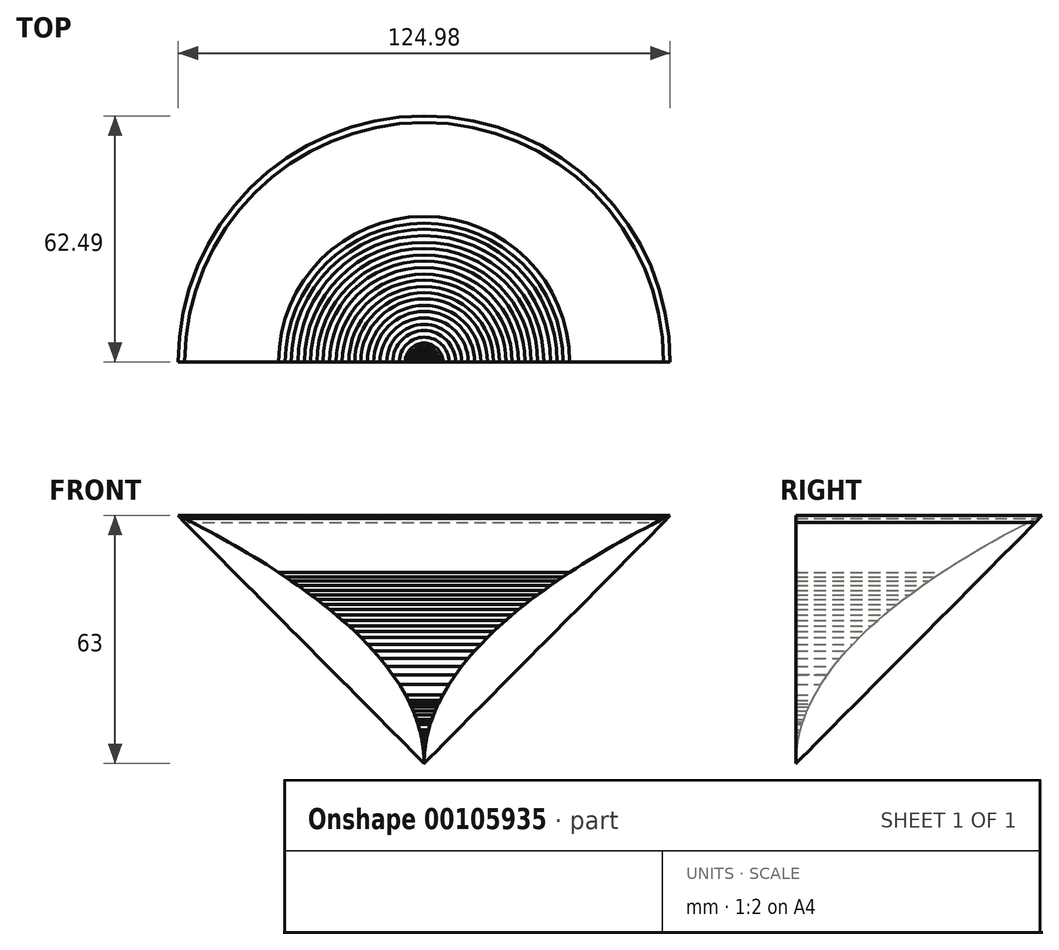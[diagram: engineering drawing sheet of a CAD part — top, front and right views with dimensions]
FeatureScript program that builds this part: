
annotation { "Feature Type Name" : "Feature", "Feature Type Description" : "" }
export const myFeature = defineFeature(function(context is Context, id is Id, definition is map)
    precondition{}
    {
        {
            var Q0;
            Q0=qCreatedBy(makeId("Front.planeOp"),FACE);
            var sketch = newSketch(context, id + "F0", { "sketchPlane" : qUnion([Q0])});
            skLineSegment(sketch, "E0", {"start": v(0, 0) * mm, "end": v(0, 71.45) * mm, "construction": true});
            skLineSegment(sketch, "E1", {"start": v(0.03, 1.24) * mm, "end": v(0.06, 1.75) * mm});
            skLineSegment(sketch, "E2", {"start": v(0.06, 1.75) * mm, "end": v(0.08, 2.15) * mm});
            skLineSegment(sketch, "E3", {"start": v(0.08, 2.15) * mm, "end": v(0.1, 2.48) * mm});
            skLineSegment(sketch, "E4", {"start": v(0.1, 2.48) * mm, "end": v(0.13, 2.77) * mm});
            skLineSegment(sketch, "E5", {"start": v(0.13, 2.77) * mm, "end": v(0.15, 3.04) * mm});
            skLineSegment(sketch, "E6", {"start": v(0.15, 3.04) * mm, "end": v(0.2, 3.5) * mm});
            skLineSegment(sketch, "E7", {"start": v(0.2, 3.5) * mm, "end": v(0.22, 3.72) * mm});
            skLineSegment(sketch, "E8", {"start": v(0.22, 3.72) * mm, "end": v(0.25, 3.92) * mm});
            skLineSegment(sketch, "E9", {"start": v(0.25, 3.92) * mm, "end": v(0.3, 4.3) * mm});
            skLineSegment(sketch, "E10", {"start": v(0.3, 4.3) * mm, "end": v(0.4, 4.96) * mm});
            skLineSegment(sketch, "E11", {"start": v(0.4, 4.96) * mm, "end": v(0.42, 5.11) * mm});
            skLineSegment(sketch, "E12", {"start": v(0.42, 5.11) * mm, "end": v(0.44, 5.26) * mm});
            skLineSegment(sketch, "E13", {"start": v(0.44, 5.26) * mm, "end": v(0.49, 5.54) * mm});
            skLineSegment(sketch, "E14", {"start": v(0.49, 5.54) * mm, "end": v(0.59, 6.07) * mm});
            skLineSegment(sketch, "E15", {"start": v(0.59, 6.07) * mm, "end": v(0.78, 7.01) * mm});
            skLineSegment(sketch, "E16", {"start": v(0.78, 7.01) * mm, "end": v(0.83, 7.23) * mm});
            skLineSegment(sketch, "E17", {"start": v(0.83, 7.23) * mm, "end": v(0.87, 7.44) * mm});
            skLineSegment(sketch, "E18", {"start": v(0.87, 7.44) * mm, "end": v(0.97, 7.84) * mm});
            skLineSegment(sketch, "E19", {"start": v(0.97, 7.84) * mm, "end": v(1.16, 8.59) * mm});
            skLineSegment(sketch, "E20", {"start": v(1.16, 8.59) * mm, "end": v(1.55, 9.92) * mm});
            skLineSegment(sketch, "E21", {"start": v(1.55, 9.92) * mm, "end": v(1.58, 10) * mm});
            skLineSegment(sketch, "E22", {"start": v(1.58, 10) * mm, "end": v(1.65, 10.25) * mm});
            skLineSegment(sketch, "E23", {"start": v(1.65, 10.25) * mm, "end": v(1.76, 10.57) * mm});
            skLineSegment(sketch, "E24", {"start": v(1.76, 10.57) * mm, "end": v(1.97, 11.18) * mm});
            skLineSegment(sketch, "E25", {"start": v(1.97, 11.18) * mm, "end": v(2.39, 12.31) * mm});
            skLineSegment(sketch, "E26", {"start": v(2.39, 12.31) * mm, "end": v(2.41, 12.38) * mm});
            skLineSegment(sketch, "E27", {"start": v(2.41, 12.38) * mm, "end": v(2.44, 12.45) * mm});
            skLineSegment(sketch, "E28", {"start": v(2.44, 12.45) * mm, "end": v(2.49, 12.58) * mm});
            skLineSegment(sketch, "E29", {"start": v(2.49, 12.58) * mm, "end": v(2.6, 12.84) * mm});
            skLineSegment(sketch, "E30", {"start": v(2.6, 12.84) * mm, "end": v(2.8, 13.35) * mm});
            skLineSegment(sketch, "E31", {"start": v(2.8, 13.35) * mm, "end": v(3.22, 14.31) * mm});
            skLineSegment(sketch, "E32", {"start": v(3.22, 14.31) * mm, "end": v(3.25, 14.37) * mm});
            skLineSegment(sketch, "E33", {"start": v(3.25, 14.37) * mm, "end": v(3.27, 14.42) * mm});
            skLineSegment(sketch, "E34", {"start": v(3.27, 14.42) * mm, "end": v(3.32, 14.53) * mm});
            skLineSegment(sketch, "E35", {"start": v(3.32, 14.53) * mm, "end": v(3.42, 14.74) * mm});
            skLineSegment(sketch, "E36", {"start": v(3.42, 14.74) * mm, "end": v(3.61, 15.16) * mm});
            skLineSegment(sketch, "E37", {"start": v(3.61, 15.16) * mm, "end": v(4, 15.96) * mm});
            skLineSegment(sketch, "E38", {"start": v(4, 15.96) * mm, "end": v(4.78, 17.45) * mm});
            skLineSegment(sketch, "E39", {"start": v(4.78, 17.45) * mm, "end": v(6.31, 20.05) * mm});
            skLineSegment(sketch, "E40", {"start": v(6.31, 20.05) * mm, "end": v(7.97, 22.53) * mm});
            skLineSegment(sketch, "E41", {"start": v(7.97, 22.53) * mm, "end": v(9.52, 24.63) * mm});
            skLineSegment(sketch, "E42", {"start": v(9.52, 24.63) * mm, "end": v(11.2, 26.71) * mm});
            skLineSegment(sketch, "E43", {"start": v(11.2, 26.71) * mm, "end": v(12.85, 28.61) * mm});
            skLineSegment(sketch, "E44", {"start": v(12.85, 28.61) * mm, "end": v(14.4, 30.28) * mm});
            skLineSegment(sketch, "E45", {"start": v(14.4, 30.28) * mm, "end": v(16.06, 31.98) * mm});
            skLineSegment(sketch, "E46", {"start": v(16.06, 31.98) * mm, "end": v(17.62, 33.5) * mm});
            skLineSegment(sketch, "E47", {"start": v(17.62, 33.5) * mm, "end": v(19.14, 34.92) * mm});
            skLineSegment(sketch, "E48", {"start": v(19.14, 34.92) * mm, "end": v(20.8, 36.4) * mm});
            skLineSegment(sketch, "E49", {"start": v(20.8, 36.4) * mm, "end": v(22.34, 37.73) * mm});
            skLineSegment(sketch, "E50", {"start": v(22.34, 37.73) * mm, "end": v(24.02, 39.12) * mm});
            skLineSegment(sketch, "E51", {"start": v(24.02, 39.12) * mm, "end": v(25.66, 40.43) * mm});
            skLineSegment(sketch, "E52", {"start": v(25.66, 40.43) * mm, "end": v(27.2, 41.62) * mm});
            skLineSegment(sketch, "E53", {"start": v(27.2, 41.62) * mm, "end": v(28.86, 42.88) * mm});
            skLineSegment(sketch, "E54", {"start": v(28.86, 42.88) * mm, "end": v(30.41, 44.02) * mm});
            skLineSegment(sketch, "E55", {"start": v(30.41, 44.02) * mm, "end": v(32.1, 45.22) * mm});
            skLineSegment(sketch, "E56", {"start": v(32.1, 45.22) * mm, "end": v(33.75, 46.37) * mm});
            skLineSegment(sketch, "E57", {"start": v(33.75, 46.37) * mm, "end": v(35.29, 47.41) * mm});
            skLineSegment(sketch, "E58", {"start": v(35.29, 47.41) * mm, "end": v(36.96, 48.52) * mm});
            skLineSegment(sketch, "E59", {"start": v(36.96, 48.52) * mm, "end": v(38.52, 49.54) * mm});
            skLineSegment(sketch, "E60", {"start": v(38.52, 49.54) * mm, "end": v(40.05, 50.51) * mm});
            skLineSegment(sketch, "E61", {"start": v(40.05, 50.51) * mm, "end": v(41.7, 51.55) * mm});
            skLineSegment(sketch, "E62", {"start": v(41.7, 51.55) * mm, "end": v(43.25, 52.5) * mm});
            skLineSegment(sketch, "E63", {"start": v(43.25, 52.5) * mm, "end": v(44.93, 53.5) * mm});
            skLineSegment(sketch, "E64", {"start": v(44.93, 53.5) * mm, "end": v(46.58, 54.47) * mm});
            skLineSegment(sketch, "E65", {"start": v(46.58, 54.47) * mm, "end": v(48.11, 55.37) * mm});
            skLineSegment(sketch, "E66", {"start": v(48.11, 55.37) * mm, "end": v(49.78, 56.32) * mm});
            skLineSegment(sketch, "E67", {"start": v(49.78, 56.32) * mm, "end": v(51.34, 57.2) * mm});
            skLineSegment(sketch, "E68", {"start": v(51.34, 57.2) * mm, "end": v(52.86, 58.03) * mm});
            skLineSegment(sketch, "E69", {"start": v(52.86, 58.03) * mm, "end": v(54.52, 58.93) * mm});
            skLineSegment(sketch, "E70", {"start": v(54.52, 58.93) * mm, "end": v(56.06, 59.76) * mm});
            skLineSegment(sketch, "E71", {"start": v(56.06, 59.76) * mm, "end": v(57.73, 60.65) * mm});
            skLineSegment(sketch, "E72", {"start": v(57.73, 60.65) * mm, "end": v(59.3, 61.46) * mm});
            skLineSegment(sketch, "E73", {"start": v(59.3, 61.46) * mm, "end": v(60.83, 62.25) * mm});
            skLineSegment(sketch, "E74", {"start": v(60.83, 62.25) * mm, "end": v(62.49, 63) * mm});
            skLineSegment(sketch, "E75", {"start": v(62.49, 63) * mm, "end": v(60.83, 61.23) * mm});
            skLineSegment(sketch, "E76", {"start": v(60.83, 61.23) * mm, "end": v(59.3, 59.69) * mm});
            skLineSegment(sketch, "E77", {"start": v(59.3, 59.69) * mm, "end": v(57.73, 58.12) * mm});
            skLineSegment(sketch, "E78", {"start": v(57.73, 58.12) * mm, "end": v(56.06, 56.43) * mm});
            skLineSegment(sketch, "E79", {"start": v(56.06, 56.43) * mm, "end": v(54.52, 54.88) * mm});
            skLineSegment(sketch, "E80", {"start": v(54.52, 54.88) * mm, "end": v(52.86, 53.21) * mm});
            skLineSegment(sketch, "E81", {"start": v(52.86, 53.21) * mm, "end": v(51.34, 51.68) * mm});
            skLineSegment(sketch, "E82", {"start": v(51.34, 51.68) * mm, "end": v(49.78, 50.1) * mm});
            skLineSegment(sketch, "E83", {"start": v(49.78, 50.1) * mm, "end": v(48.11, 48.43) * mm});
            skLineSegment(sketch, "E84", {"start": v(48.11, 48.43) * mm, "end": v(46.58, 46.89) * mm});
            skLineSegment(sketch, "E85", {"start": v(46.58, 46.89) * mm, "end": v(44.93, 45.23) * mm});
            skLineSegment(sketch, "E86", {"start": v(44.93, 45.23) * mm, "end": v(43.25, 43.54) * mm});
            skLineSegment(sketch, "E87", {"start": v(43.25, 43.54) * mm, "end": v(41.7, 41.98) * mm});
            skLineSegment(sketch, "E88", {"start": v(41.7, 41.98) * mm, "end": v(40.05, 40.31) * mm});
            skLineSegment(sketch, "E89", {"start": v(40.05, 40.31) * mm, "end": v(38.52, 38.77) * mm});
            skLineSegment(sketch, "E90", {"start": v(38.52, 38.77) * mm, "end": v(36.96, 37.2) * mm});
            skLineSegment(sketch, "E91", {"start": v(36.96, 37.2) * mm, "end": v(35.29, 35.52) * mm});
            skLineSegment(sketch, "E92", {"start": v(35.29, 35.52) * mm, "end": v(33.75, 33.97) * mm});
            skLineSegment(sketch, "E93", {"start": v(33.75, 33.97) * mm, "end": v(32.1, 32.3) * mm});
            skLineSegment(sketch, "E94", {"start": v(32.1, 32.3) * mm, "end": v(30.41, 30.61) * mm});
            skLineSegment(sketch, "E95", {"start": v(30.41, 30.61) * mm, "end": v(28.86, 29.05) * mm});
            skLineSegment(sketch, "E96", {"start": v(28.86, 29.05) * mm, "end": v(27.2, 27.37) * mm});
            skLineSegment(sketch, "E97", {"start": v(27.2, 27.37) * mm, "end": v(25.66, 25.83) * mm});
            skLineSegment(sketch, "E98", {"start": v(25.66, 25.83) * mm, "end": v(24.02, 24.18) * mm});
            skLineSegment(sketch, "E99", {"start": v(24.02, 24.18) * mm, "end": v(22.34, 22.49) * mm});
            skLineSegment(sketch, "E100", {"start": v(22.34, 22.49) * mm, "end": v(20.8, 20.93) * mm});
            skLineSegment(sketch, "E101", {"start": v(20.8, 20.93) * mm, "end": v(19.14, 19.27) * mm});
            skLineSegment(sketch, "E102", {"start": v(19.14, 19.27) * mm, "end": v(17.62, 17.73) * mm});
            skLineSegment(sketch, "E103", {"start": v(17.62, 17.73) * mm, "end": v(16.06, 16.16) * mm});
            skLineSegment(sketch, "E104", {"start": v(16.06, 16.16) * mm, "end": v(14.4, 14.48) * mm});
            skLineSegment(sketch, "E105", {"start": v(14.4, 14.48) * mm, "end": v(12.85, 12.93) * mm});
            skLineSegment(sketch, "E106", {"start": v(12.85, 12.93) * mm, "end": v(11.2, 11.27) * mm});
            skLineSegment(sketch, "E107", {"start": v(11.2, 11.27) * mm, "end": v(9.52, 9.58) * mm});
            skLineSegment(sketch, "E108", {"start": v(9.52, 9.58) * mm, "end": v(7.97, 8.02) * mm});
            skLineSegment(sketch, "E109", {"start": v(7.97, 8.02) * mm, "end": v(6.31, 6.35) * mm});
            skLineSegment(sketch, "E110", {"start": v(6.31, 6.35) * mm, "end": v(4.78, 4.81) * mm});
            skLineSegment(sketch, "E111", {"start": v(4.78, 4.81) * mm, "end": v(3.22, 3.24) * mm});
            skLineSegment(sketch, "E112", {"start": v(3.22, 3.24) * mm, "end": v(1.55, 1.55) * mm});
            skLineSegment(sketch, "E113", {"start": v(1.55, 1.55) * mm, "end": v(0.78, 0.78) * mm});
            skLineSegment(sketch, "E114", {"start": v(0.78, 0.78) * mm, "end": v(0.4, 0.4) * mm});
            skLineSegment(sketch, "E115", {"start": v(0.4, 0.4) * mm, "end": v(0.2, 0.2) * mm});
            skLineSegment(sketch, "E116", {"start": v(0.2, 0.2) * mm, "end": v(0, 0) * mm});
            skLineSegment(sketch, "E117", {"start": v(0, 0) * mm, "end": v(0.03, 1.24) * mm});
            skSolve(sketch);
        }
        {
            var Q0;
            Q0=makeQuery(id+"F0.imprint","IMPRINT",FACE,{"disambiguationData":[TD([[makeQuery(id+"F0.imprint","IMPRINT",EDGE,{"derivedFrom":sQuery(id+"F0.wireOp",EDGE,"E1")}),-1.0]])]});
            var Q1;
            Q1=sQuery(id+"F0.wireOp",EDGE,"6cd0e086-f095-49ee-bd14-0fb4bcdf7f62");
            var Q2;
            Q2=sQuery(id+"F0.wireOp",EDGE,"32b9a501-6f23-47c1-bb88-d8d60de19fad");
            var Q3;
            Q3=sQuery(id+"F0.wireOp",EDGE,"0ab19f62-0243-4b47-b9d7-9aae8800fd34");
            var Q4;
            Q4=sQuery(id+"F0.wireOp",EDGE,"2ca119f5-cc54-42c8-b016-c2b29b4d06b1");
            var Q5;
            Q5=sQuery(id+"F0.wireOp",EDGE,"ab69b40b-8ee6-484d-87df-27fd168b416f");
            var Q6;
            Q6=sQuery(id+"F0.wireOp",EDGE,"d2e7aa8f-2c4b-49e1-838e-42aa97e10c56");
            var Q7;
            Q7=sQuery(id+"F0.wireOp",EDGE,"f10a260a-276a-4d93-a087-e43724df36d4");
            var Q8;
            Q8=sQuery(id+"F0.wireOp",EDGE,"7f855701-bcad-4d86-bddb-f70fd6bfc80a");
            var Q9;
            Q9=sQuery(id+"F0.wireOp",EDGE,"08ec54eb-994a-4fb6-b174-f5e7ee304757");
            var Q10;
            Q10=sQuery(id+"F0.wireOp",EDGE,"a5612133-c2e1-4ef4-8b9f-3609430e4b8a");
            var Q11;
            Q11=sQuery(id+"F0.wireOp",EDGE,"418e4bf5-dd02-48d2-a26f-4e3a346c8d43");
            var Q12;
            Q12=sQuery(id+"F0.wireOp",EDGE,"b8dc723f-4637-4b02-823a-4596eccecf82");
            var Q13;
            Q13=sQuery(id+"F0.wireOp",EDGE,"00636bc2-a381-4cdd-9ff9-5b5603eccf9d");
            var Q14;
            Q14=sQuery(id+"F0.wireOp",EDGE,"7af5d30f-ebfe-441f-bb73-a1719346f9de");
            var Q15;
            Q15=sQuery(id+"F0.wireOp",EDGE,"36245651-de9b-4736-b1f9-26fced389540");
            var Q16;
            Q16=sQuery(id+"F0.wireOp",EDGE,"9174d457-cd45-4d7f-b965-8e008558b735");
            var Q17;
            Q17=sQuery(id+"F0.wireOp",EDGE,"9525182e-9101-41d7-9018-a1a02df04e69");
            var Q18;
            Q18=sQuery(id+"F0.wireOp",EDGE,"fbbc2854-f1f6-44d0-9c84-9e8661b49e57");
            var Q19;
            Q19=sQuery(id+"F0.wireOp",EDGE,"c3a2e51d-9eb8-41d9-a87d-9a92de79b262");
            var Q20;
            Q20=sQuery(id+"F0.wireOp",EDGE,"6bbd898d-2acf-4b63-ae52-23587b2590af");
            var Q21;
            Q21=sQuery(id+"F0.wireOp",EDGE,"80403143-b7bb-4d31-9be5-d1759cc80739");
            var Q22;
            Q22=sQuery(id+"F0.wireOp",EDGE,"f25b2a2c-930c-46b5-9bfa-9cd2fbff0c83");
            var Q23;
            Q23=sQuery(id+"F0.wireOp",EDGE,"b865bc6a-677d-4d4f-932f-e9aefe434b45");
            var Q24;
            Q24=sQuery(id+"F0.wireOp",EDGE,"2116273a-b908-41fd-b9aa-db6f0ef41ba9");
            var Q25;
            Q25=sQuery(id+"F0.wireOp",EDGE,"b2ffb272-9dcf-4623-b1d1-8ed364749e69");
            var Q26;
            Q26=sQuery(id+"F0.wireOp",EDGE,"b4d96bac-3605-4eab-8db4-85aa0a498f1e");
            var Q27;
            Q27=sQuery(id+"F0.wireOp",EDGE,"1515ba95-663b-468d-b96c-22abc7b3f79b");
            var Q28;
            Q28=sQuery(id+"F0.wireOp",EDGE,"3f1fde4d-109f-498a-a201-36b045cca48a");
            var Q29;
            Q29=sQuery(id+"F0.wireOp",EDGE,"356e45f0-cfad-41af-a3ec-996ddad23460");
            var Q30;
            Q30=sQuery(id+"F0.wireOp",EDGE,"68fa8913-69cc-4ca1-82e6-e40190e9411c");
            var Q31;
            Q31=sQuery(id+"F0.wireOp",EDGE,"5685c587-d4e7-4eb6-beec-dd555197c508");
            var Q32;
            Q32=sQuery(id+"F0.wireOp",EDGE,"e32970ef-e5eb-4fed-b033-dcb7383ce353");
            var Q33;
            Q33=sQuery(id+"F0.wireOp",EDGE,"7f2a3c70-c066-46c7-bac0-3dfb802e3b35");
            var Q34;
            Q34=sQuery(id+"F0.wireOp",EDGE,"d2da8106-e0f2-4740-92ea-ccbd867c5f05");
            var Q35;
            Q35=sQuery(id+"F0.wireOp",EDGE,"add72adc-a49c-4cb2-9938-cdb23ad0af4a");
            var Q36;
            Q36=sQuery(id+"F0.wireOp",EDGE,"6a777c45-0ae2-4cab-bbba-c9cd995294f1");
            var Q37;
            Q37=sQuery(id+"F0.wireOp",EDGE,"c228eeea-3b64-47fa-b97c-331c723c14b7");
            var Q38;
            Q38=sQuery(id+"F0.wireOp",EDGE,"395098cc-0f29-4a3d-839d-d5eab6b9f8f6");
            var Q39;
            Q39=sQuery(id+"F0.wireOp",EDGE,"181f3d82-3629-4897-b77f-4c8848b632a5");
            var Q40;
            Q40=sQuery(id+"F0.wireOp",EDGE,"c7ccb2a9-1d45-46e1-b1b9-4b5ecab7b650");
            var Q41;
            Q41=sQuery(id+"F0.wireOp",EDGE,"bf075199-5a07-4ae9-962d-6314e180a530");
            var Q42;
            Q42=sQuery(id+"F0.wireOp",EDGE,"76886f05-ee9d-419f-8532-b242ab29ebb3");
            var Q43;
            Q43=sQuery(id+"F0.wireOp",EDGE,"f07c7b62-e916-4f94-864d-a85d08dad243");
            var Q44;
            Q44=sQuery(id+"F0.wireOp",EDGE,"39223102-3a32-4200-9aec-4477b4b4de44");
            var Q45;
            Q45=sQuery(id+"F0.wireOp",EDGE,"43d0a0f2-a6c7-4702-8e31-672eb94790b6");
            var Q46;
            Q46=sQuery(id+"F0.wireOp",EDGE,"7623a77c-cf58-45cb-b00f-866a358ce328");
            var Q47;
            Q47=sQuery(id+"F0.wireOp",EDGE,"32b33bd1-1cb3-402a-a8d1-c9da59b7d9db");
            var Q48;
            Q48=sQuery(id+"F0.wireOp",EDGE,"6ca921c3-4361-433c-8c39-55e94d84a59d");
            var Q49;
            Q49=sQuery(id+"F0.wireOp",EDGE,"48faec90-704a-4a37-8a98-1a9c80e3b44e");
            var Q50;
            Q50=sQuery(id+"F0.wireOp",EDGE,"9af8efc3-a8d1-405c-9059-f8faaa2b8f43");
            var Q51;
            Q51=sQuery(id+"F0.wireOp",EDGE,"1329a4fc-b186-475f-b203-a901afba9a69");
            var Q52;
            Q52=sQuery(id+"F0.wireOp",EDGE,"fccac4c7-3ed9-4ce5-ad8b-ede4d597a9d8");
            var Q53;
            Q53=sQuery(id+"F0.wireOp",EDGE,"2d6af91c-cbc1-4309-b3c7-a9f612d22b46");
            var Q54;
            Q54=sQuery(id+"F0.wireOp",EDGE,"c0f88d67-35d7-400a-bc80-a9fc9052a76f");
            var Q55;
            Q55=sQuery(id+"F0.wireOp",EDGE,"13014262-3845-466c-997c-4b1b5d220b85");
            var Q56;
            Q56=sQuery(id+"F0.wireOp",EDGE,"48568539-6200-46ff-bab0-8303b6930a13");
            var Q57;
            Q57=sQuery(id+"F0.wireOp",EDGE,"98a91311-34dd-4d03-bd07-0819f0495df8");
            var Q58;
            Q58=sQuery(id+"F0.wireOp",EDGE,"3583fb7b-63ad-41cb-b8b8-8cb26a940dac");
            var Q59;
            Q59=sQuery(id+"F0.wireOp",EDGE,"fefdcaa8-b758-4b29-9bea-e3188ad52759");
            var Q60;
            Q60=sQuery(id+"F0.wireOp",EDGE,"67b2c278-f296-4df3-801d-c68f92e39153");
            var Q61;
            Q61=sQuery(id+"F0.wireOp",EDGE,"0a15342a-3a2c-49ed-8f05-ac1ed5891651");
            var Q62;
            Q62=sQuery(id+"F0.wireOp",EDGE,"dce7d2aa-6561-4adb-a796-b7b1930769ed");
            var Q63;
            Q63=sQuery(id+"F0.wireOp",EDGE,"4e09961f-fe0a-403c-a5c9-d9112d7a3957");
            var Q64;
            Q64=sQuery(id+"F0.wireOp",EDGE,"572beb88-f651-4b68-8d29-c4148b90713c");
            var Q65;
            Q65=sQuery(id+"F0.wireOp",EDGE,"137ae89f-9f74-4a93-99b2-a19355498890");
            var Q66;
            Q66=sQuery(id+"F0.wireOp",EDGE,"2cfc42b0-43f6-4077-81bd-d5c6913363b1");
            var Q67;
            Q67=sQuery(id+"F0.wireOp",EDGE,"84f63fe7-a7c1-42b1-97fd-f71986a5366e");
            var Q68;
            Q68=sQuery(id+"F0.wireOp",EDGE,"9dcc372c-3c07-435e-b519-3f0781d2b983");
            var Q69;
            Q69=sQuery(id+"F0.wireOp",EDGE,"78a2393d-9690-4013-91ef-c6b91cd97901");
            var Q70;
            Q70=sQuery(id+"F0.wireOp",EDGE,"2ed5d36b-0ec2-4eba-88c0-e75aeadd8ae3");
            var Q71;
            Q71=sQuery(id+"F0.wireOp",EDGE,"5a31f5a9-2e82-4e29-8f45-6dc4fd328668");
            var Q72;
            Q72=sQuery(id+"F0.wireOp",EDGE,"09f0dd61-81a5-4896-b91d-417e8f37575d");
            var Q73;
            Q73=sQuery(id+"F0.wireOp",EDGE,"3f812a27-3b59-4eed-b2f4-40afadd15fa8");
            var Q74;
            Q74=sQuery(id+"F0.wireOp",EDGE,"6b0f5955-a4f0-4227-8d57-a41b44beba1f");
            var Q75;
            Q75=sQuery(id+"F0.wireOp",EDGE,"c938ad5b-75a9-4010-b756-059c32605906");
            var Q76;
            Q76=sQuery(id+"F0.wireOp",EDGE,"ec079bdb-ea27-4997-8836-05392c6045e0");
            var Q77;
            Q77=sQuery(id+"F0.wireOp",EDGE,"a6f52760-9543-4489-b3a6-5ce92bfd3c08");
            var Q78;
            Q78=sQuery(id+"F0.wireOp",EDGE,"4b679cf0-3c00-475e-8df6-f6ade93deaa6");
            var Q79;
            Q79=sQuery(id+"F0.wireOp",EDGE,"4c356e91-b964-4982-bfc1-02ad547de3b3");
            var Q80;
            Q80=sQuery(id+"F0.wireOp",EDGE,"08e088a4-c56e-4f10-813e-be4f049c5b76");
            var Q81;
            Q81=sQuery(id+"F0.wireOp",EDGE,"59c83a3e-1ea1-4c51-8c56-9a878b44d4cb");
            var Q82;
            Q82=sQuery(id+"F0.wireOp",EDGE,"17712dbd-5605-461e-93e5-0bb03f775670");
            var Q83;
            Q83=sQuery(id+"F0.wireOp",EDGE,"961d6043-29b9-4277-8ae2-64cd68e63820");
            var Q84;
            Q84=sQuery(id+"F0.wireOp",EDGE,"961e9428-0606-426c-b518-49b9529d7fed");
            var Q85;
            Q85=sQuery(id+"F0.wireOp",EDGE,"e9903241-ff48-4a06-b7a4-94d682a9480b");
            var Q86;
            Q86=sQuery(id+"F0.wireOp",EDGE,"fc12d687-f38c-462e-969c-e45fa5e76c45");
            var Q87;
            Q87=sQuery(id+"F0.wireOp",EDGE,"e39b9d96-bab4-40ca-8a10-92499f8d2be3");
            var Q88;
            Q88=sQuery(id+"F0.wireOp",EDGE,"0cff3415-95f2-4afc-b6e1-037d20eb3730");
            var Q89;
            Q89=sQuery(id+"F0.wireOp",EDGE,"b707cd78-946f-4bd4-8840-26f174feb00c");
            var Q90;
            Q90=sQuery(id+"F0.wireOp",EDGE,"88cda176-fb2f-449d-b64b-6b50f711ec8a");
            var Q91;
            Q91=sQuery(id+"F0.wireOp",EDGE,"bd4fe06c-6bad-46b4-a88b-ec94b67a4c70");
            var Q92;
            Q92=sQuery(id+"F0.wireOp",EDGE,"cbb06e03-c999-4148-aa16-954b55afef36");
            var Q93;
            Q93=sQuery(id+"F0.wireOp",EDGE,"07b2797e-1b9b-4b26-9dbd-d07ca5d4feaa");
            var Q94;
            Q94=sQuery(id+"F0.wireOp",EDGE,"ed610fc8-1701-4f4b-94c3-c6a34d4d9202");
            var Q95;
            Q95=sQuery(id+"F0.wireOp",EDGE,"eec642e5-7255-45fc-9db4-03261cf94d9a");
            var Q96;
            Q96=sQuery(id+"F0.wireOp",EDGE,"13a30e3b-af0a-4f2c-8af2-a0571a1f4525");
            var Q97;
            Q97=sQuery(id+"F0.wireOp",EDGE,"2b14b9bc-7ad1-4c61-b380-f0cd198d4729");
            var Q98;
            Q98=sQuery(id+"F0.wireOp",EDGE,"fc41495b-5a6c-4837-8155-86ce8040ff6e");
            var Q99;
            Q99=sQuery(id+"F0.wireOp",EDGE,"9e231f45-9dea-498f-b230-aa831b055d47");
            var Q100;
            Q100=sQuery(id+"F0.wireOp",EDGE,"412cd04a-ae6d-42f2-aede-6bfde44f6cb9");
            var Q101;
            Q101=sQuery(id+"F0.wireOp",EDGE,"1e1094b9-5462-4261-a438-cdb2ca7576de");
            var Q102;
            Q102=sQuery(id+"F0.wireOp",EDGE,"811fc2df-8b63-46c9-8ad8-45ed09e117c1");
            var Q103;
            Q103=sQuery(id+"F0.wireOp",EDGE,"57162d4b-a903-403a-8676-7f7f2f5f1bd2");
            var Q104;
            Q104=sQuery(id+"F0.wireOp",EDGE,"53b33fde-b057-4959-9f1c-3b7dd6977b76");
            var Q105;
            Q105=sQuery(id+"F0.wireOp",EDGE,"38582804-de92-4dba-b73b-c960f2b2eadf");
            var Q106;
            Q106=sQuery(id+"F0.wireOp",EDGE,"c7c96c91-c102-41a1-a907-521ad09825cc");
            var Q107;
            Q107=sQuery(id+"F0.wireOp",EDGE,"53203cdc-9a3b-4c92-af52-1bcac2f7ff32");
            var Q108;
            Q108=sQuery(id+"F0.wireOp",EDGE,"b6ef23df-cee8-488e-8c46-d5cabb0ec031");
            var Q109;
            Q109=sQuery(id+"F0.wireOp",EDGE,"8ad53e4a-a3b0-4098-a4d3-9a8a57d3f7d3");
            var Q110;
            Q110=sQuery(id+"F0.wireOp",EDGE,"609456eb-d379-4178-8fde-78bb7a74957d");
            var Q111;
            Q111=sQuery(id+"F0.wireOp",EDGE,"41d71823-22bc-4bd5-b4ee-9574a2ad43fc");
            var Q112;
            Q112=sQuery(id+"F0.wireOp",EDGE,"3d42aacd-27ec-49ed-877b-a5dbab20bba3");
            var Q113;
            Q113=sQuery(id+"F0.wireOp",EDGE,"e5302213-2089-424f-9c95-027443b08a4e");
            var Q114;
            Q114=sQuery(id+"F0.wireOp",EDGE,"7204529a-c635-4b10-8ead-91a96f8ad75c");
            var Q115;
            Q115=sQuery(id+"F0.wireOp",EDGE,"f04bd4f7-50ed-41db-a464-22d31b791a0d");
            var Q116;
            Q116=sQuery(id+"F0.wireOp",EDGE,"f226d074-4344-4b88-93cd-f1ad3baee5e7");
            var Q117;
            Q117=sQuery(id+"F0.wireOp",EDGE,"8a24e8c1-b523-4f9a-842c-170059644050");
            var Q118;
            Q118=sQuery(id+"F0.wireOp",EDGE,"E0");
            revolve(context, id + "F1", {"entities" : qUnion([Q0]), "surfaceEntities" : qUnion([Q1, Q2, Q3, Q4, Q5, Q6, Q7, Q8, Q9, Q10, Q11, Q12, Q13, Q14, Q15, Q16, Q17, Q18, Q19, Q20, Q21, Q22, Q23, Q24, Q25, Q26, Q27, Q28, Q29, Q30, Q31, Q32, Q33, Q34, Q35, Q36, Q37, Q38, Q39, Q40, Q41, Q42, Q43, Q44, Q45, Q46, Q47, Q48, Q49, Q50, Q51, Q52, Q53, Q54, Q55, Q56, Q57, Q58, Q59, Q60, Q61, Q62, Q63, Q64, Q65, Q66, Q67, Q68, Q69, Q70, Q71, Q72, Q73, Q74, Q75, Q76, Q77, Q78, Q79, Q80, Q81, Q82, Q83, Q84, Q85, Q86, Q87, Q88, Q89, Q90, Q91, Q92, Q93, Q94, Q95, Q96, Q97, Q98, Q99, Q100, Q101, Q102, Q103, Q104, Q105, Q106, Q107, Q108, Q109, Q110, Q111, Q112, Q113, Q114, Q115, Q116, Q117]), "axis" : qUnion([Q118]), "revolveType" : RevolveType.ONE_DIRECTION, "angle" : 180 * degree});
        }
    });
